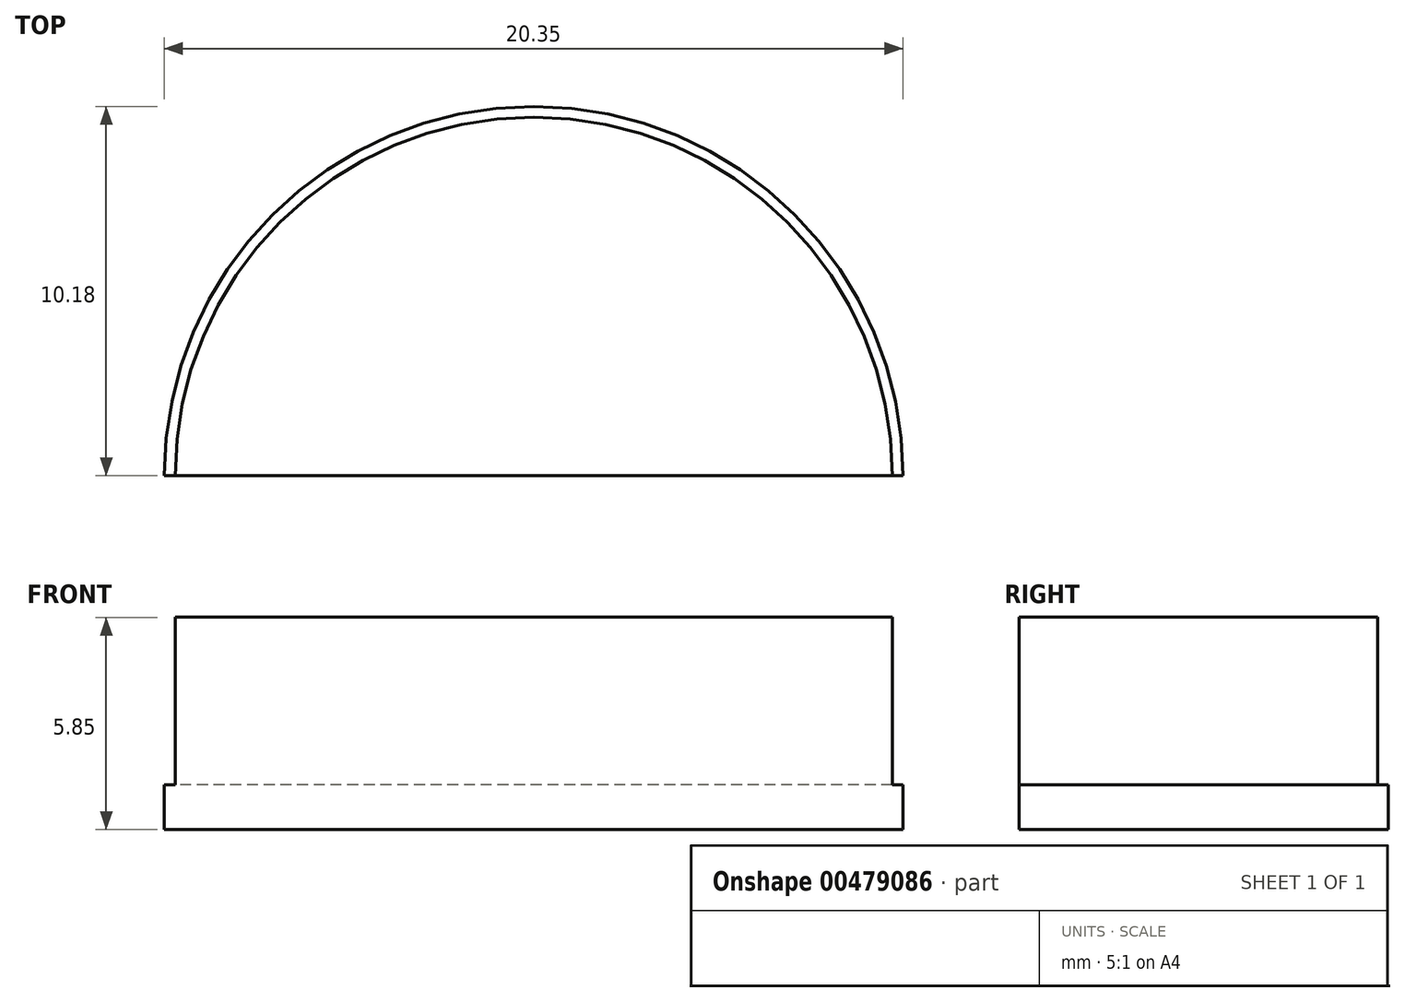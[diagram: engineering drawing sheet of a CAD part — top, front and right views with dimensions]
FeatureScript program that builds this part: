
annotation { "Feature Type Name" : "Feature", "Feature Type Description" : "" }
export const myFeature = defineFeature(function(context is Context, id is Id, definition is map)
    precondition{}
    {
        {
            var Q0;
            Q0=qCreatedBy(makeId("Front.planeOp"),FACE);
            var sketch = newSketch(context, id + "F0", { "sketchPlane" : qUnion([Q0])});
            skLineSegment(sketch, "E0", {"start": v(7.44, -0.86) * mm, "end": v(-2.74, -0.86) * mm});
            skLineSegment(sketch, "E1", {"start": v(-2.74, -0.86) * mm, "end": v(-2.74, 0.37) * mm});
            skLineSegment(sketch, "E2", {"start": v(-2.74, 0.37) * mm, "end": v(-2.44, 0.37) * mm});
            skLineSegment(sketch, "E3", {"start": v(-2.44, 0.37) * mm, "end": v(-2.44, 5) * mm});
            skLineSegment(sketch, "E4", {"start": v(-2.44, 5) * mm, "end": v(7.44, 5) * mm});
            skLineSegment(sketch, "E5", {"start": v(7.44, 5) * mm, "end": v(7.44, -0.86) * mm});
            skSolve(sketch);
        }
        {
            var Q0;
            Q0=makeQuery(id+"F0.imprint","IMPRINT",FACE,{"disambiguationData":[TD([[makeQuery(id+"F0.imprint","IMPRINT",EDGE,{"derivedFrom":sQuery(id+"F0.wireOp",EDGE,"E0")}),-1.0]])]});
            var Q1;
            Q1=sQuery(id+"F0.wireOp",EDGE,"E5");
            revolve(context, id + "F1", {"entities" : qUnion([Q0]), "axis" : qUnion([Q1]), "revolveType" : RevolveType.ONE_DIRECTION, "angle" : 180 * degree});
        }
    });
